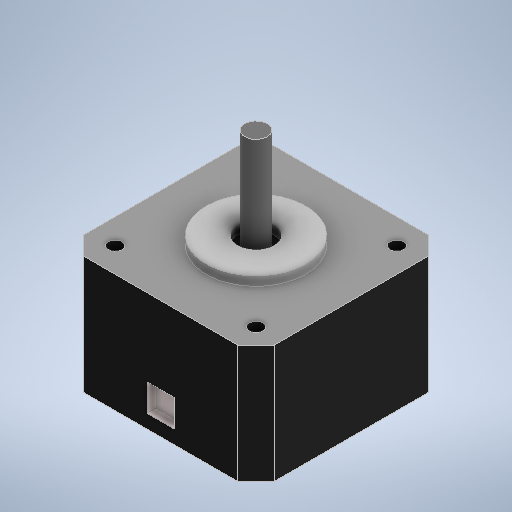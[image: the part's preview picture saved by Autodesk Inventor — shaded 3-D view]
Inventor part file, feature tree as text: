
AUTODESK INVENTOR PART (.ipt)
format: ipt  version: 2025.1 (Build 291241000, 241)  size: 302,080 bytes
history: native  units: mm
features: extrude x5, sketch x2
ambient origin geometry x8: Origin, YZ Plane, XZ Plane, XY Plane, X Axis, Y Axis, Z Axis, Center Point
bodies: Solid1 (feature_tree)
feature tree (7):
  sketch  "Sketch1"  dims[d1=31.0mm d2=31.0mm]
  extrude  "Extrusion1"  Depth=31.0mm
  extrude  "Extrusion2"  Depth=3.0mm
  extrude  "Extrusion3"  Depth=3.0mm
  extrude  "Extrusion4"  Depth=3.0mm
  extrude  "Extrusion5"  Depth=3.0mm
  sketch  "Sketch2"  dims[d3=31.0mm d4=31.0mm d5=3.0mm d6=3.0mm d7=3.0mm d8=3.0mm d9=26.0mm d10=0.0mm d11=22.0mm d12=2.0mm d13=0.0mm d14=8.0mm d15=2.0mm d16=0.0mm d17=6.0mm d18=6.0mm d22=2.0mm d23=0.0mm d32=5.0mm d33=20.0mm d34=2.0mm d35=0.0mm d36=0.0mm d37=15.5mm d38=42.0mm d39=42.0mm d40=15.5mm d41=21.0mm d42=21.0mm d43=34.0mm d44=34.0mm d45=135.0deg d46=3.0mm]
